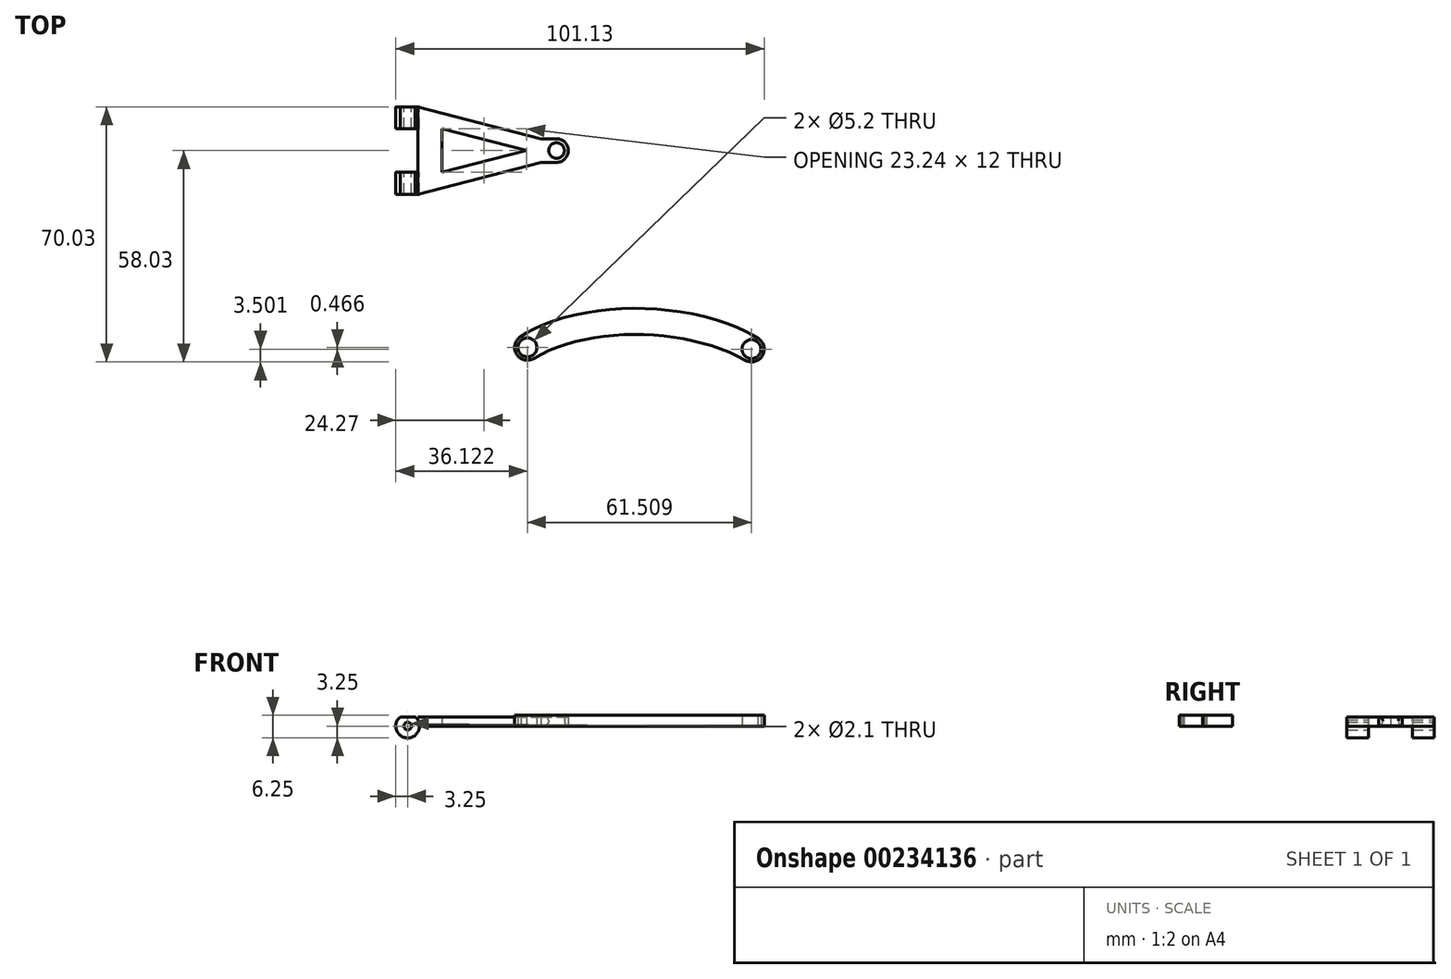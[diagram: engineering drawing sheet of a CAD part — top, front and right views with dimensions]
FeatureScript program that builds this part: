
annotation { "Feature Type Name" : "Feature", "Feature Type Description" : "" }
export const myFeature = defineFeature(function(context is Context, id is Id, definition is map)
    precondition{}
    {
        {
            var Q0;
            Q0=qCreatedBy(makeId("Top.planeOp"),FACE);
            var sketch = newSketch(context, id + "F0", { "sketchPlane" : qUnion([Q0])});
            skLineSegment(sketch, "E0", {"start": v(-21.43, 12) * mm, "end": v(-21.43, 0) * mm});
            skLineSegment(sketch, "E1", {"start": v(12.46, 2.75) * mm, "end": v(16.69, 2.75) * mm});
            skArc(sketch, "E2", {"start": v(16.69, 2.75) * mm, "mid": v(19.94, 6) * mm, "end": v(16.69, 9.25) * mm});
            skLineSegment(sketch, "E3", {"start": v(16.69, 9.25) * mm, "end": v(12.46, 9.25) * mm});
            skLineSegment(sketch, "E4", {"start": v(12.46, 9.25) * mm, "end": v(-21.43, 18) * mm});
            skLineSegment(sketch, "E5", {"start": v(-21.43, 18) * mm, "end": v(-27.43, 18) * mm});
            skLineSegment(sketch, "E6", {"start": v(-27.43, 18) * mm, "end": v(-27.43, 12) * mm});
            skLineSegment(sketch, "E7", {"start": v(-27.43, 12) * mm, "end": v(-21.43, 12) * mm});
            skLineSegment(sketch, "E8", {"start": v(-21.43, 0) * mm, "end": v(-27.43, 0) * mm});
            skLineSegment(sketch, "E9", {"start": v(-27.43, 0) * mm, "end": v(-27.43, -6) * mm});
            skLineSegment(sketch, "E10", {"start": v(-27.43, -6) * mm, "end": v(-21.43, -6) * mm});
            skLineSegment(sketch, "E11", {"start": v(-21.43, -6) * mm, "end": v(12.46, 2.75) * mm});
            skCircle(sketch, "E12", {"center": v(16.69, 6) * mm, "radius": 2.15 * mm});
            skLineSegment(sketch, "E13", {"start": v(-14.78, 12) * mm, "end": v(8.46, 6) * mm});
            skLineSegment(sketch, "E14", {"start": v(8.46, 6) * mm, "end": v(-14.78, 0) * mm});
            skLineSegment(sketch, "E15", {"start": v(-14.78, 0) * mm, "end": v(-14.78, 12) * mm});
            skLineSegment(sketch, "E16", {"start": v(-21.43, 18) * mm, "end": v(-21.43, 12) * mm});
            skLineSegment(sketch, "E17", {"start": v(-21.43, 0) * mm, "end": v(-21.43, -6) * mm});
            skLineSegment(sketch, "E18", {"start": v(-24.18, 12) * mm, "end": v(-24.18, 0) * mm});
            skLineSegment(sketch, "E19", {"start": v(-25.23, 0) * mm, "end": v(-25.23, -6) * mm});
            skLineSegment(sketch, "E20", {"start": v(-23.13, -6) * mm, "end": v(-23.13, 0) * mm});
            skLineSegment(sketch, "E21", {"start": v(-25.23, 12) * mm, "end": v(-25.23, 18) * mm});
            skLineSegment(sketch, "E22", {"start": v(-23.13, 18) * mm, "end": v(-23.13, 12) * mm});
            skSolve(sketch);
        }
        {
            var Q0;
            Q0=makeQuery(id+"F0.imprint","IMPRINT",FACE,{"disambiguationData":[TD([[makeQuery(id+"F0.imprint","IMPRINT",EDGE,{"derivedFrom":sQuery(id+"F0.wireOp",EDGE,"E0")}),1.0]])]});
            extrude(context, id + "F1", {"entities" : qUnion([Q0]), "depth" : 2.5 * mm});
        }
        {
            var Q0;
            {var subQ0=sQuery(id+"F0.wireOp",EDGE,"E6");Q0=makeQuery(id+"F0.imprint","IMPRINT",FACE,{"disambiguationData":[TD([[makeQuery(id+"F0.imprint","IMPRINT",EDGE,{"derivedFrom":subQ0}),1.0]])]});}
            var Q1;
            {var subQ0=sQuery(id+"F0.wireOp",EDGE,"E9");Q1=makeQuery(id+"F0.imprint","IMPRINT",FACE,{"disambiguationData":[TD([[makeQuery(id+"F0.imprint","IMPRINT",EDGE,{"derivedFrom":subQ0}),1.0]])]});}
            var Q2;
            Q2=sQuery(id+"F0.wireOp",EDGE,"E18");
            revolve(context, id + "F2", {"operationType" : NewBodyOperationType.ADD, "entities" : qUnion([Q0, Q1]), "axis" : qUnion([Q2]), "revolveType" : RevolveType.FULL});
        }
        {
            var Q0;
            Q0=makeQuery(id+"F1.opExtrude","CAP_FACE",FACE,{"disambiguationData":[OSD([sQuery(id+"F0.wireOp",EDGE,"E0"),sQuery(id+"F0.wireOp",EDGE,"E1"),sQuery(id+"F0.wireOp",EDGE,"E2"),sQuery(id+"F0.wireOp",EDGE,"E3"),sQuery(id+"F0.wireOp",EDGE,"E4"),sQuery(id+"F0.wireOp",EDGE,"E11"),sQuery(id+"F0.wireOp",EDGE,"E12"),sQuery(id+"F0.wireOp",EDGE,"E13"),sQuery(id+"F0.wireOp",EDGE,"E14"),sQuery(id+"F0.wireOp",EDGE,"E15"),sQuery(id+"F0.wireOp",EDGE,"E16"),sQuery(id+"F0.wireOp",EDGE,"E17")])],"isStart":false});
            var sketch = newSketch(context, id + "F3", { "sketchPlane" : qUnion([Q0])});
            skLineSegment(sketch, "E23.bottom", {"start": v(-17.68, -8.15) * mm, "end": v(-32.18, -8.15) * mm});
            skLineSegment(sketch, "E23.top", {"start": v(-17.68, 19.48) * mm, "end": v(-32.18, 19.48) * mm});
            skLineSegment(sketch, "E23.left", {"start": v(-17.68, -8.15) * mm, "end": v(-17.68, 19.48) * mm});
            skLineSegment(sketch, "E23.right", {"start": v(-32.18, -8.15) * mm, "end": v(-32.18, 19.48) * mm});
            skSolve(sketch);
        }
        {
            var Q0;
            {var subQ4=sQuery(id+"F3.wireOp",EDGE,"E23.bottom");Q0=makeQuery(id+"F3.imprint","IMPRINT",FACE,{"disambiguationData":[TD([[makeQuery(id+"F3.imprint","IMPRINT",EDGE,{"derivedFrom":subQ4}),-1.0]])]});}
            extrude(context, id + "F4", {"entities" : qUnion([Q0]), "operationType" : NewBodyOperationType.REMOVE, "depth" : 25 * mm});
        }
        {
            var Q0;
            Q0=makeQuery(id+"F1.opExtrude","CAP_EDGE",EDGE,{"disambiguationData":[OSD([sQuery(id+"F0.wireOp",EDGE,"E12")])],"isStart":false});
            fillet(context, id + "F5", {"entities" : qUnion([Q0]), "radius" : 1 * mm, "tangentPropagation" : true, "allowEdgeOverflow" : false});
        }
        {
            var Q0;
            Q0=qCreatedBy(makeId("Top.planeOp"),FACE);
            var sketch = newSketch(context, id + "F6", { "sketchPlane" : qUnion([Q0])});
            skLineSegment(sketch, "E24", {"start": v(-71.89, -29.15) * mm, "end": v(-15.89, -29.15) * mm});
            skArc(sketch, "E25", {"start": v(-15.89, -29.15) * mm, "mid": v(-12.39, -25.65) * mm, "end": v(-15.89, -22.15) * mm});
            skArc(sketch, "E26", {"start": v(-71.89, -22.15) * mm, "mid": v(-75.39, -25.65) * mm, "end": v(-71.89, -29.15) * mm});
            skLineSegment(sketch, "E27", {"start": v(-71.89, -22.15) * mm, "end": v(-15.89, -22.15) * mm});
            skFitSpline(sketch, "E28", {"points": [v(10.48, -51.07) * mm, v(68.48, -51.58) * mm], "startDerivative": vector(46.43, 27.54) * mm, "endDerivative": vector(47.97, -27.13) * mm});
            skFitSpline(sketch, "E29.0", {"points": [v(6.9, -45.05) * mm, v(9.23, -43.67) * mm, v(14.19, -41.35) * mm, v(22.24, -39) * mm, v(30.7, -37.69) * mm, v(39.38, -37.34) * mm, v(48.06, -37.92) * mm, v(56.54, -39.43) * mm, v(64.6, -41.87) * mm, v(69.58, -44.16) * mm, v(71.92, -45.48) * mm]});
            skLineSegment(sketch, "E30", {"start": v(71.92, -45.48) * mm, "end": v(68.48, -51.58) * mm});
            skLineSegment(sketch, "E31", {"start": v(10.48, -51.07) * mm, "end": v(6.9, -45.05) * mm});
            skArc(sketch, "E32", {"start": v(68.48, -51.58) * mm, "mid": v(73.25, -50.25) * mm, "end": v(71.92, -45.48) * mm});
            skArc(sketch, "E33", {"start": v(6.9, -45.05) * mm, "mid": v(5.68, -49.85) * mm, "end": v(10.48, -51.07) * mm});
            skCircle(sketch, "E34", {"center": v(70.2, -48.53) * mm, "radius": 2.6 * mm});
            skCircle(sketch, "E35", {"center": v(8.7, -48.06) * mm, "radius": 2.6 * mm});
            skSolve(sketch);
        }
        {
            var Q0;
            {var subQ2=sQuery(id+"F6.wireOp",EDGE,"E28");Q0=makeQuery(id+"F6.imprint","IMPRINT",FACE,{"disambiguationData":[TD([[makeQuery(id+"F6.imprint","IMPRINT",EDGE,{"derivedFrom":subQ2}),1.0]])]});}
            var Q1;
            {var subQ0=sQuery(id+"F6.wireOp",EDGE,"E33");Q1=makeQuery(id+"F6.imprint","IMPRINT",FACE,{"disambiguationData":[TD([[makeQuery(id+"F6.imprint","IMPRINT",EDGE,{"derivedFrom":subQ0}),1.0]])]});}
            var Q2;
            {var subQ0=sQuery(id+"F6.wireOp",EDGE,"E32");Q2=makeQuery(id+"F6.imprint","IMPRINT",FACE,{"disambiguationData":[TD([[makeQuery(id+"F6.imprint","IMPRINT",EDGE,{"derivedFrom":subQ0}),1.0]])]});}
            extrude(context, id + "F7", {"entities" : qUnion([Q0, Q1, Q2]), "depth" : 3 * mm});
        }
        {
            var Q0;
            Q0=makeQuery(id+"F1.opExtrude","CAP_EDGE",EDGE,{"disambiguationData":[OSD([sQuery(id+"F0.wireOp",EDGE,"E12")])],"isStart":true});
            fillet(context, id + "F8", {"entities" : qUnion([Q0]), "radius" : 1.5 * mm, "tangentPropagation" : true, "allowEdgeOverflow" : false});
        }
    });
